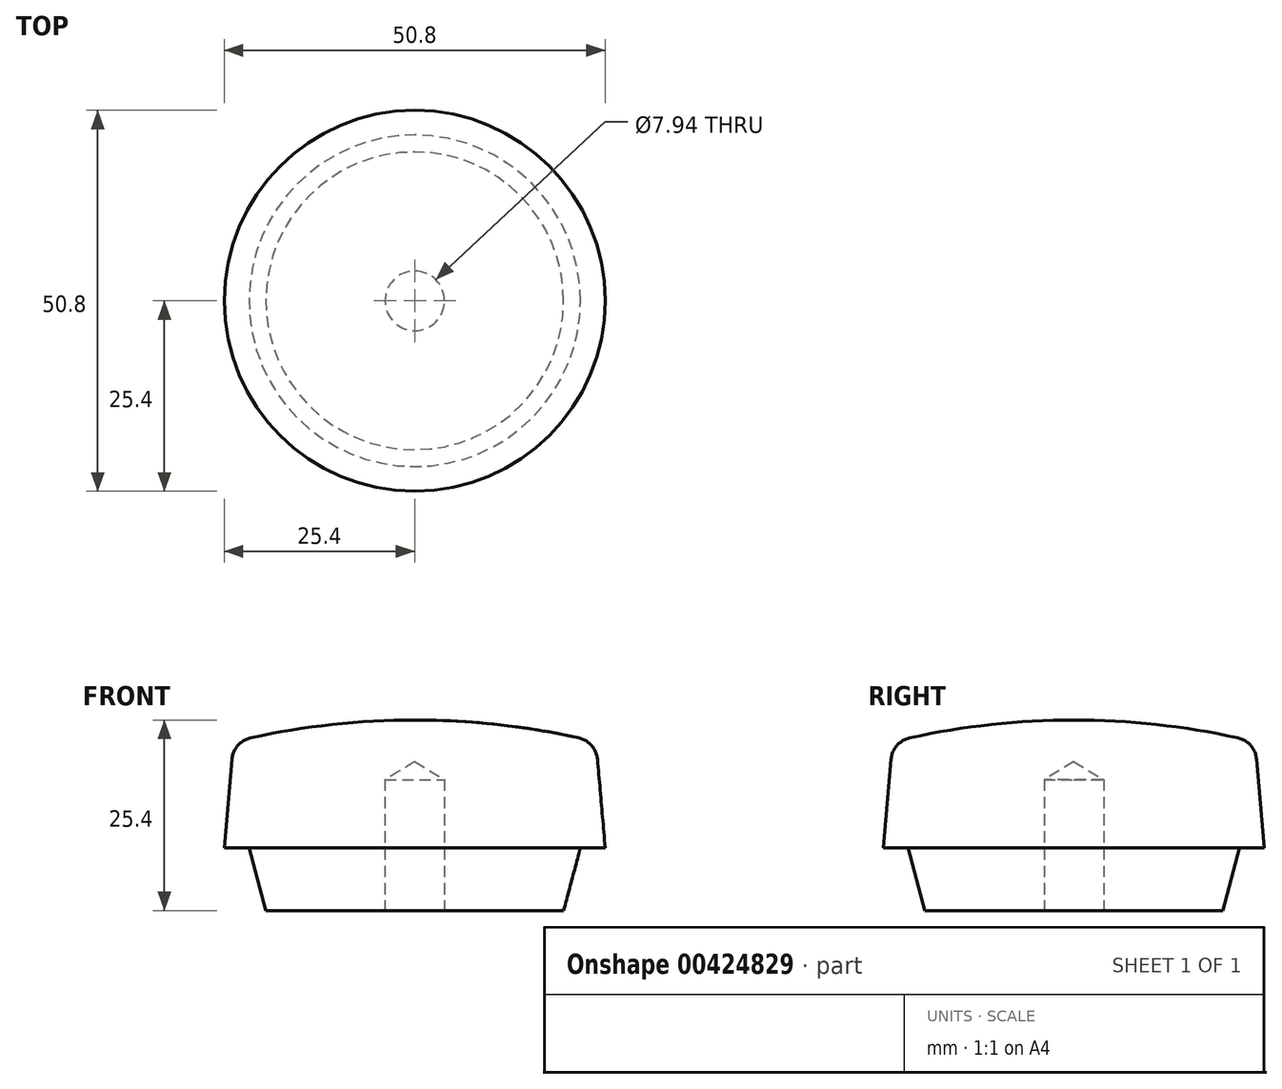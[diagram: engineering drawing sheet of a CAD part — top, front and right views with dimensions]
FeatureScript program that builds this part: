
annotation { "Feature Type Name" : "Feature", "Feature Type Description" : "" }
export const myFeature = defineFeature(function(context is Context, id is Id, definition is map)
    precondition{}
    {
        {
            var Q0;
            Q0=qCreatedBy(makeId("Front.planeOp"),FACE);
            var sketch = newSketch(context, id + "F0", { "sketchPlane" : qUnion([Q0])});
            skFitSpline(sketch, "E0.0.4", {"points": [v(19.85, 0) * mm, v(6.62, 0) * mm, v(-6.62, 0) * mm, v(-19.85, 0) * mm]});
            skLineSegment(sketch, "E1", {"start": v(19.85, 0) * mm, "end": v(22.1, 8.38) * mm});
            skLineSegment(sketch, "E2", {"start": v(0, 25.4) * mm, "end": v(0, 0) * mm});
            skLineSegment(sketch, "E3", {"start": v(22.1, 8.38) * mm, "end": v(25.4, 8.38) * mm});
            skLineSegment(sketch, "E4", {"start": v(25.4, 8.38) * mm, "end": v(24.17, 22.48) * mm});
            skArc(sketch, "E5", {"start": v(24.17, 22.48) * mm, "mid": v(12.17, 24.67) * mm, "end": v(0, 25.4) * mm});
            skPoint(sketch, "E6", {"position": v(0, 0) * mm});
            skSolve(sketch);
        }
        {
            var Q0;
            Q0=makeQuery(id+"F0.imprint","IMPRINT",FACE,{"disambiguationData":[TD([[makeQuery(id+"F0.imprint","IMPRINT",EDGE,{"derivedFrom":sQuery(id+"F0.wireOp",EDGE,"E0.0.4")}),-1.0]])]});
            var Q1;
            Q1=sQuery(id+"F0.wireOp",EDGE,"E2");
            revolve(context, id + "F1", {"entities" : qUnion([Q0]), "axis" : qUnion([Q1]), "revolveType" : RevolveType.FULL});
        }
        {
            var Q0;
            Q0=makeQuery(id+"F1.opRevolve","SWEPT_FACE",FACE,{"disambiguationData":[OSD([sQuery(id+"F0.wireOp",EDGE,"E0.0.4")])]});
            var sketch = newSketch(context, id + "F2", { "sketchPlane" : qUnion([Q0])});
            skPoint(sketch, "E7", {"position": v(0, 0) * mm});
            skSolve(sketch);
        }
        {
            var Q0;
            Q0=sQuery(id+"F2.wireOp",VERTEX,"E7");
            var Q1;
            Q1=makeQuery(id+"F1.opRevolve","SWEPT_BODY",BODY,{"disambiguationData":[OSD([sQuery(id+"F0.wireOp",EDGE,"E0.0.4"),sQuery(id+"F0.wireOp",EDGE,"E1"),sQuery(id+"F0.wireOp",EDGE,"E2"),sQuery(id+"F0.wireOp",EDGE,"E3"),sQuery(id+"F0.wireOp",EDGE,"E4"),sQuery(id+"F0.wireOp",EDGE,"E5")])]});
            hole(context, id + "F3", {"style" : HoleStyle.SIMPLE, "endStyle" : HoleEndStyle.BLIND, "standardTappedOrClearance" : lookupTablePath({ "standard" : "ANSI", "engagement" : "75%", "pitch" : "16 tpi", "size" : "3/8", "type" : "Tapped" }), "standardBlindInLast" : lookupTablePath({ "standard" : "ANSI", "engagement" : "75%", "pitch" : "16 tpi", "size" : "3/8", "type" : "Tapped" }), "holeDiameter" : 7.94 * mm, "showTappedDepth" : true, "holeDepth" : 17.46 * mm, "isTappedThrough" : true, "tappedDepth" : 12.7 * mm, "tapClearance" : 3, "locations" : qUnion([Q0]), "scope" : qUnion([Q1]), "majorDiameter" : 9.53 * mm});
        }
        {
            var Q0;
            Q0=makeQuery(id+"F1.opRevolve","SWEPT_EDGE",EDGE,{"disambiguationData":[OSD([sQuery(id+"F0.wireOp",EDGE,"E4"),sQuery(id+"F0.wireOp",EDGE,"E5")])]});
            fillet(context, id + "F4", {"entities" : qUnion([Q0]), "radius" : 3.17 * mm, "tangentPropagation" : true, "allowEdgeOverflow" : false});
        }
    });
